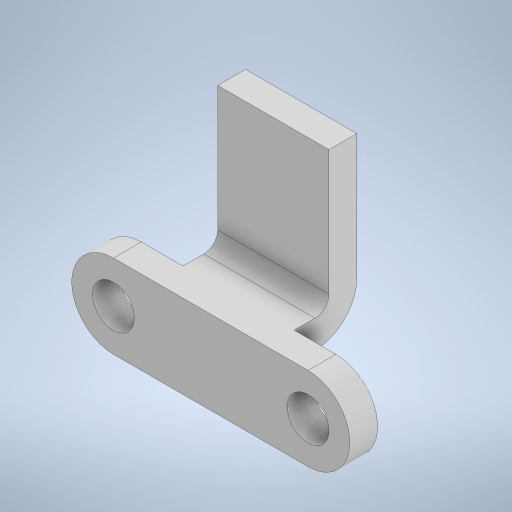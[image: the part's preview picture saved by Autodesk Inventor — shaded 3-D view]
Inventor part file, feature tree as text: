
AUTODESK INVENTOR PART (.ipt)
format: ipt  version: 2024 (Build 280153000, 153)  size: 260,096 bytes
history: native  units: in
note: dims shown in document units (in); Inventor stores cm internally (conversion verified against a paired STEP export)
features: extrude x2, sketch x2
ambient origin geometry x8: Origin, YZ Plane, XZ Plane, XY Plane, X Axis, Y Axis, Z Axis, Center Point
bodies: Solid1 (feature_tree)
feature tree (4):
  extrude  "Extrusion1"  Depth=3.5in
  extrude  "Extrusion2"  Depth=1.5in
  sketch  "Sketch1"  dims[d0=7.0in d1=3.5in]
  sketch  "Sketch2"  dims[d2=1.5in d3=1.5in d4=1.5in d5=1.0in d6=0.0in d7=0.5in d8=1.5in d9=5.0in d10=2.25in d11=1.0in d12=1.0in d13=4.0in d14=0.0in]
